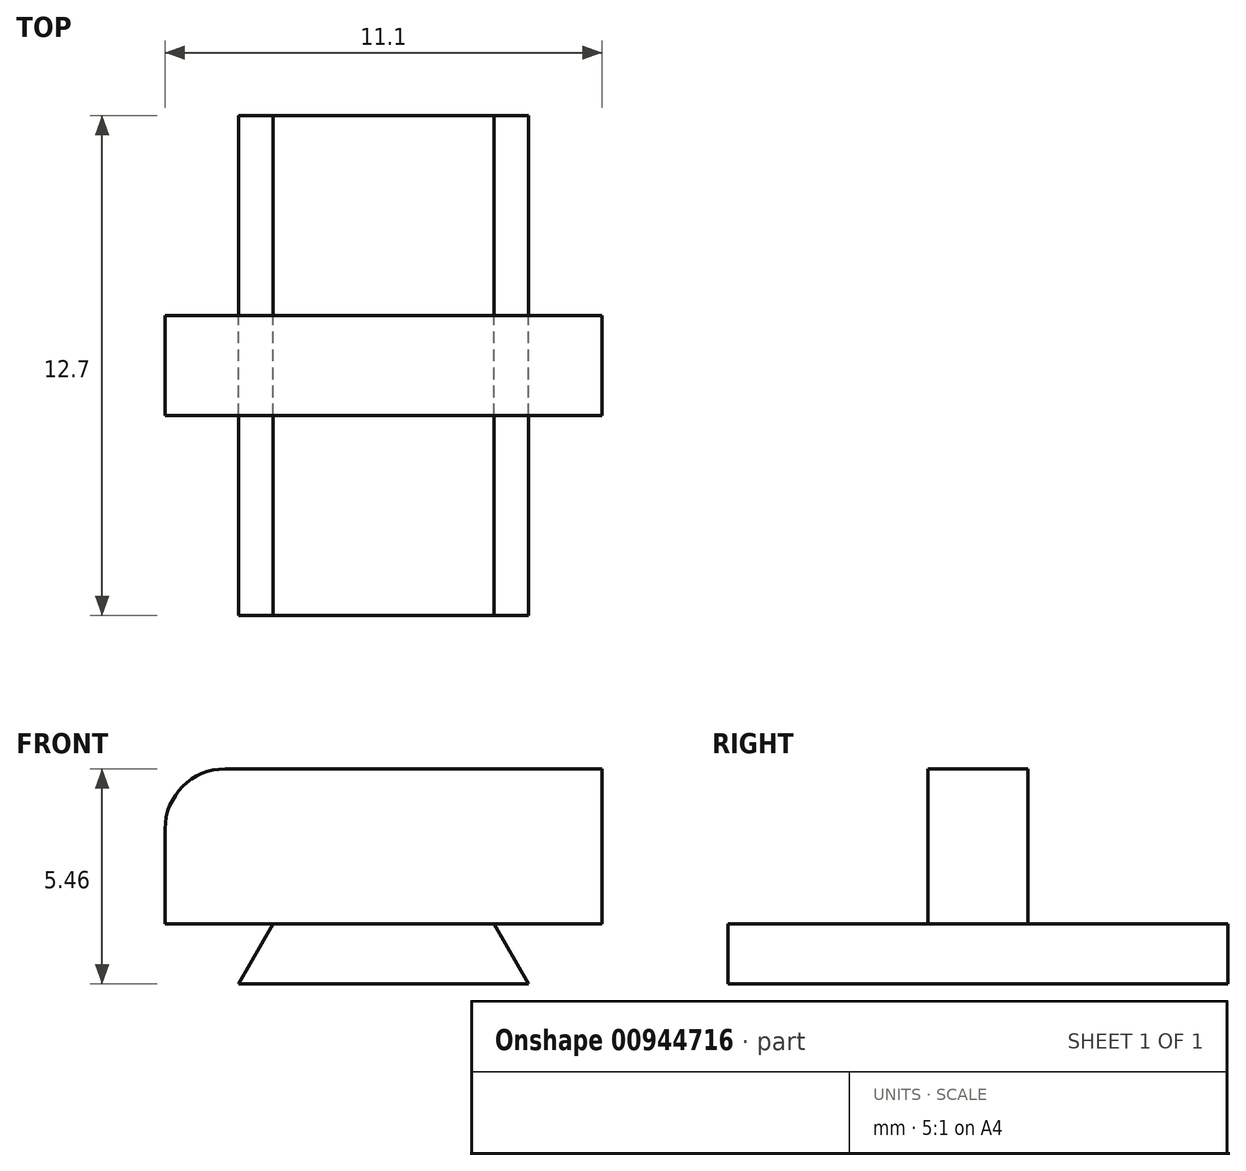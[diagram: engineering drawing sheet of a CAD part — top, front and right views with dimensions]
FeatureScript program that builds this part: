
annotation { "Feature Type Name" : "Feature", "Feature Type Description" : "" }
export const myFeature = defineFeature(function(context is Context, id is Id, definition is map)
    precondition{}
    {
        {
            var Q0;
            Q0=qCreatedBy(makeId("Front.planeOp"),FACE);
            var sketch = newSketch(context, id + "F0", { "sketchPlane" : qUnion([Q0])});
            skLineSegment(sketch, "E0", {"start": v(-3.74, 0) * mm, "end": v(3.62, 0) * mm});
            skLineSegment(sketch, "E1", {"start": v(3.62, 0) * mm, "end": v(2.74, 1.52) * mm});
            skLineSegment(sketch, "E2", {"start": v(2.74, 1.52) * mm, "end": v(5.49, 1.52) * mm});
            skLineSegment(sketch, "E3", {"start": v(5.49, 1.52) * mm, "end": v(5.49, 5.46) * mm});
            skLineSegment(sketch, "E4", {"start": v(5.49, 5.46) * mm, "end": v(-5.6, 5.46) * mm});
            skLineSegment(sketch, "E5", {"start": v(-5.6, 5.46) * mm, "end": v(-5.6, 1.52) * mm});
            skLineSegment(sketch, "E6", {"start": v(-5.6, 1.52) * mm, "end": v(-2.86, 1.52) * mm});
            skLineSegment(sketch, "E7", {"start": v(-2.86, 1.52) * mm, "end": v(-3.74, 0) * mm});
            skSolve(sketch);
        }
        {
            var Q0;
            Q0=makeQuery(id+"F0.imprint","IMPRINT",FACE,{"disambiguationData":[TD([[makeQuery(id+"F0.imprint","IMPRINT",EDGE,{"derivedFrom":sQuery(id+"F0.wireOp",EDGE,"E0")}),1.0]])]});
            extrude(context, id + "F1", {"entities" : qUnion([Q0]), "depth" : 12.7 * mm, "offsetDistance" : 25.4 * mm});
        }
        {
            var Q0;
            Q0=makeQuery(id+"F1.opExtrude","SWEPT_FACE",FACE,{"disambiguationData":[OSD([sQuery(id+"F0.wireOp",EDGE,"E3")])]});
            var sketch = newSketch(context, id + "F2", { "sketchPlane" : qUnion([Q0])});
            skLineSegment(sketch, "E8", {"start": v(-12.7, 1.52) * mm, "end": v(-7.62, 1.52) * mm});
            skLineSegment(sketch, "E9", {"start": v(-7.62, 1.52) * mm, "end": v(-7.62, 5.46) * mm});
            skLineSegment(sketch, "E10", {"start": v(-7.62, 5.46) * mm, "end": v(-5.08, 5.46) * mm});
            skLineSegment(sketch, "E11", {"start": v(-5.08, 5.46) * mm, "end": v(-5.08, 1.52) * mm});
            skLineSegment(sketch, "E12", {"start": v(-5.08, 1.52) * mm, "end": v(0, 1.52) * mm});
            skLineSegment(sketch, "E13", {"start": v(0, 1.52) * mm, "end": v(0, 0) * mm});
            skLineSegment(sketch, "E14", {"start": v(0, 0) * mm, "end": v(-12.7, 0) * mm});
            skLineSegment(sketch, "E15", {"start": v(-12.7, 0) * mm, "end": v(-12.7, 1.52) * mm});
            skSolve(sketch);
        }
        {
            var Q0;
            {var subQ0=sQuery(id+"F2.wireOp",EDGE,"E9");Q0=makeQuery(id+"F2.imprint","IMPRINT",FACE,{"disambiguationData":[TD([[makeQuery(id+"F2.imprint","IMPRINT",EDGE,{"derivedFrom":subQ0}),-1.0]])]});}
            var Q1;
            {var subQ1=sQuery(id+"F2.wireOp",EDGE,"E8");Q1=makeQuery(id+"F2.imprint","IMPRINT",FACE,{"disambiguationData":[TD([[makeQuery(id+"F2.imprint","IMPRINT",EDGE,{"derivedFrom":subQ1}),-1.0]])]});}
            extrude(context, id + "F3", {"entities" : qUnion([Q0, Q1]), "operationType" : NewBodyOperationType.INTERSECT, "oppositeDirection" : true, "depth" : 25.4 * mm, "offsetDistance" : 25.4 * mm});
        }
        {
            var Q0;
            Q0=makeQuery(id+"F1.opExtrude","SWEPT_EDGE",EDGE,{"disambiguationData":[OSD([sQuery(id+"F0.wireOp",EDGE,"E4"),sQuery(id+"F0.wireOp",EDGE,"E5")])]});
            fillet(context, id + "F4", {"entities" : qUnion([Q0]), "radius" : 1.52 * mm, "tangentPropagation" : true, "allowEdgeOverflow" : false});
        }
    });
